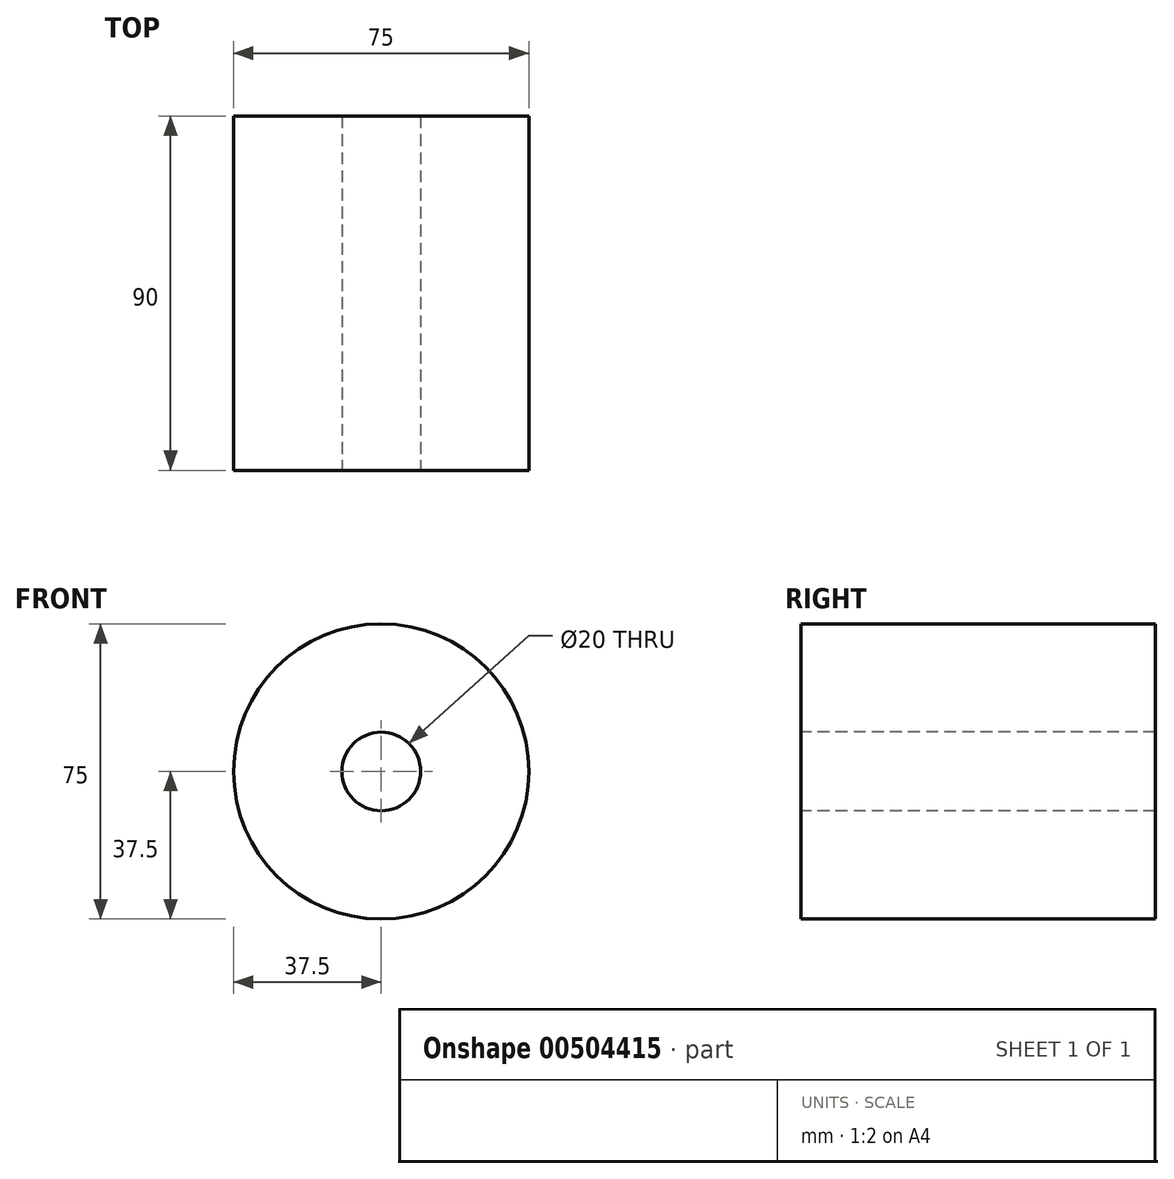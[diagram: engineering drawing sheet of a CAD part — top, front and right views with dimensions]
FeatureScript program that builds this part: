
annotation { "Feature Type Name" : "Feature", "Feature Type Description" : "" }
export const myFeature = defineFeature(function(context is Context, id is Id, definition is map)
    precondition{}
    {
        {
            var Q0;
            Q0=qCreatedBy(makeId("Right.planeOp"),FACE);
            var sketch = newSketch(context, id + "F0", { "sketchPlane" : qUnion([Q0])});
            skLineSegment(sketch, "E0", {"start": v(-60.4, 0) * mm, "end": v(51.45, 0) * mm, "construction": true});
            skLineSegment(sketch, "E1.bottom", {"start": v(-45, 37.5) * mm, "end": v(45, 37.5) * mm});
            skLineSegment(sketch, "E1.top", {"start": v(-45, 10) * mm, "end": v(45, 10) * mm});
            skLineSegment(sketch, "E1.left", {"start": v(-45, 37.5) * mm, "end": v(-45, 10) * mm});
            skLineSegment(sketch, "E1.right", {"start": v(45, 37.5) * mm, "end": v(45, 10) * mm});
            skSolve(sketch);
        }
        {
            var Q0;
            Q0=makeQuery(id+"F0.imprint","IMPRINT",FACE,{"disambiguationData":[TD([[makeQuery(id+"F0.imprint","IMPRINT",EDGE,{"derivedFrom":sQuery(id+"F0.wireOp",EDGE,"E1.bottom")}),-1.0]])]});
            var Q1;
            Q1=sQuery(id+"F0.wireOp",EDGE,"E0");
            revolve(context, id + "F1", {"entities" : qUnion([Q0]), "axis" : qUnion([Q1]), "revolveType" : RevolveType.FULL});
        }
    });
